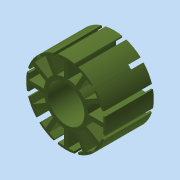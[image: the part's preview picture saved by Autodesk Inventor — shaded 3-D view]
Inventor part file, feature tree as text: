
AUTODESK INVENTOR PART (.ipt)
format: ipt  version: 2015 (Build 190159000, 159)  size: 203,776 bytes
history: native  units: in
note: dims shown in document units (in); Inventor stores cm internally (conversion verified against a paired STEP export)
features: extrude x1, pattern_circular x1, sketch x1
ambient origin geometry x8: Origin, YZ Plane, XZ Plane, XY Plane, X Axis, Y Axis, Z Axis, Center Point
bodies: Solid1 (feature_tree)
feature tree (3):
  extrude  "Extrusion1"  Depth=1.1811in
  pattern_circular  "Circular Pattern1"  [2 undecoded]
  sketch  "Sketch1"  dims[d0=0.9055in d1=1.9685in d2=0.1649in d3=1.1024in d4=4.7244in d6=360.0deg d8=1.1811in d9=0.0in d10=4.7244in d11=360.0deg]
note: 2 required parameter values undecoded (feature->parameter linkage not recoverable at this tier; creation-order binding heuristic only, values carry confidence <= 0.55)
